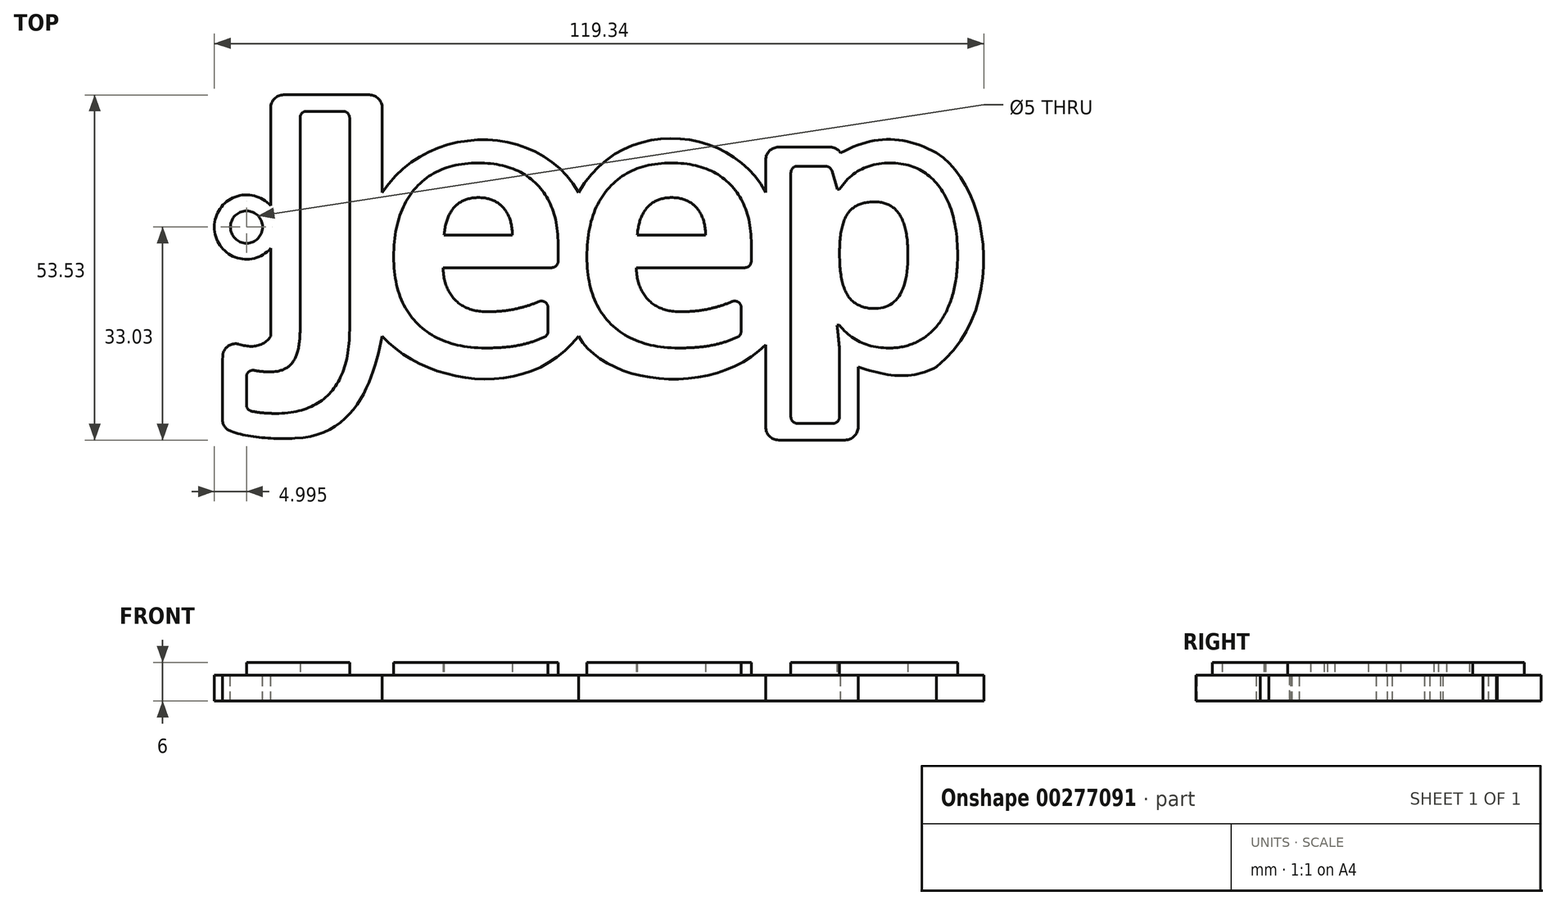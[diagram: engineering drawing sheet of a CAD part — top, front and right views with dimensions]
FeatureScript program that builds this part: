
annotation { "Feature Type Name" : "Feature", "Feature Type Description" : "" }
export const myFeature = defineFeature(function(context is Context, id is Id, definition is map)
    precondition{}
    {
        {
            var Q0;
            Q0=qCreatedBy(makeId("Top.planeOp"),FACE);
            var sketch = newSketch(context, id + "F0", { "sketchPlane" : qUnion([Q0])});
            skText(sketch, "E0", { "text": "Jeep", "fontName": "OpenSans-Bold.ttf"});
            skFitSpline(sketch, "E1", {"points": [v(-56.8, 0) * mm, v(-56.8, 20.5) * mm], "startDerivative": vector(0, 20.5) * mm, "endDerivative": vector(0, 20.5) * mm});
            skFitSpline(sketch, "E2", {"points": [v(-56.8, 20.5) * mm, v(-39.5, 20.5) * mm], "startDerivative": vector(15.4, 0) * mm, "endDerivative": vector(15.4, 0) * mm});
            skFitSpline(sketch, "E3", {"points": [v(-39.5, 5.36) * mm, v(-39.5, 20.5) * mm], "startDerivative": vector(0, 15.14) * mm, "endDerivative": vector(0, 15.14) * mm});
            skFitSpline(sketch, "E4", {"points": [v(-39.5, 5.36) * mm, v(-9.05, 5.36) * mm], "startDerivative": vector(21.09, 32.44) * mm, "endDerivative": vector(18.36, -32.95) * mm});
            skFitSpline(sketch, "E5", {"points": [v(-9.05, 5.36) * mm, v(19.99, 5.36) * mm], "startDerivative": vector(20.19, 35.94) * mm, "endDerivative": vector(16.2, -31.1) * mm});
            skFitSpline(sketch, "E6", {"points": [v(19.99, 5.36) * mm, v(19.99, 12.4) * mm], "startDerivative": vector(0, 7.03) * mm, "endDerivative": vector(0, 7.03) * mm});
            skFitSpline(sketch, "E7", {"points": [v(19.99, 12.4) * mm, v(31.61, 12.4) * mm], "startDerivative": vector(11.63, 0) * mm, "endDerivative": vector(11.63, 0) * mm});
            skFitSpline(sketch, "E8", {"points": [v(31.61, 12.4) * mm, v(31.61, 11.04) * mm], "startDerivative": vector(0, -1.35) * mm, "endDerivative": vector(0, -1.35) * mm});
            skFitSpline(sketch, "E9", {"points": [v(31.61, 11.5) * mm, v(46.48, 11.5) * mm], "startDerivative": vector(15.41, 8.38) * mm, "endDerivative": vector(15.41, -8.38) * mm});
            skFitSpline(sketch, "E10", {"points": [v(46.48, 11.5) * mm, v(46.48, -21.68) * mm], "startDerivative": vector(24.33, -15.14) * mm, "endDerivative": vector(-33.84, -27.42) * mm});
            skFitSpline(sketch, "E11", {"points": [v(46.48, -21.68) * mm, v(34.32, -21.68) * mm], "startDerivative": vector(-10.86, -6.04) * mm, "endDerivative": vector(-13.79, 4.87) * mm});
            skFitSpline(sketch, "E12", {"points": [v(34.32, -21.68) * mm, v(34.32, -33.03) * mm], "startDerivative": vector(0, -11.36) * mm, "endDerivative": vector(0, -11.36) * mm});
            skFitSpline(sketch, "E13", {"points": [v(34.32, -33.03) * mm, v(19.99, -33.03) * mm], "startDerivative": vector(-14.33, 0) * mm, "endDerivative": vector(-14.33, 0) * mm});
            skFitSpline(sketch, "E14", {"points": [v(19.99, -33.03) * mm, v(19.99, -18.26) * mm], "startDerivative": vector(0, 14.77) * mm, "endDerivative": vector(0, 14.77) * mm});
            skFitSpline(sketch, "E15", {"points": [v(19.99, -18.26) * mm, v(-9.05, -16.94) * mm], "startDerivative": vector(-23.52, -24.04) * mm, "endDerivative": vector(-13.5, 23.5) * mm});
            skFitSpline(sketch, "E16", {"points": [v(-9.05, -16.94) * mm, v(-39.5, -16.94) * mm], "startDerivative": vector(-22.79, -29.43) * mm, "endDerivative": vector(-21.9, 23.52) * mm});
            skFitSpline(sketch, "E17", {"points": [v(-39.5, -16.94) * mm, v(-53.01, -32.76) * mm], "startDerivative": vector(-4.06, -19.47) * mm, "endDerivative": vector(-29.09, -1.3) * mm});
            skFitSpline(sketch, "E18", {"points": [v(-53.01, -32.76) * mm, v(-64.27, -31.14) * mm], "startDerivative": vector(-13.04, -0.66) * mm, "endDerivative": vector(-8.11, 4.06) * mm});
            skFitSpline(sketch, "E19", {"points": [v(-64.27, -31.14) * mm, v(-64.27, -16.94) * mm], "startDerivative": vector(-0.27, 11.09) * mm, "endDerivative": vector(-0.27, 11.09) * mm});
            skFitSpline(sketch, "E20", {"points": [v(-64.27, -16.94) * mm, v(-56.8, -16.94) * mm], "startDerivative": vector(6.49, -4.06) * mm, "endDerivative": vector(5.7, 8.11) * mm});
            skFitSpline(sketch, "E21", {"points": [v(-56.8, -16.94) * mm, v(-56.8, 0) * mm], "startDerivative": vector(0, 19.51) * mm, "endDerivative": vector(0, 19.51) * mm});
            skCircle(sketch, "E22", {"center": v(-60.54, 0) * mm, "radius": 5 * mm});
            skCircle(sketch, "E23", {"center": v(-60.54, 0) * mm, "radius": 2.5 * mm});
            skLineSegment(sketch, "E24", {"start": v(-58.04, 0) * mm, "end": v(-55.54, 0) * mm});
            const initialGuessF0  = {"E0": [-0.0568, -0.01826, 1, 0, 0.03652]};
            skSetInitialGuess(sketch, initialGuessF0);
            skSolve(sketch);
        }
        {
            var Q0;
            Q0=makeQuery(id+"F0.imprint","IMPRINT",FACE,{"disambiguationData":[TD([[makeQuery(id+"F0.imprint","IMPRINT",EDGE,{"derivedFrom":sQuery(id+"F0.wireOp",EDGE,"E0.sketch_text.stroke-0")}),1.0]])]});
            var Q1;
            Q1=makeQuery(id+"F0.imprint","IMPRINT",FACE,{"disambiguationData":[TD([[makeQuery(id+"F0.imprint","IMPRINT",EDGE,{"derivedFrom":sQuery(id+"F0.wireOp",EDGE,"E0.sketch_text.stroke-0")}),-1.0]])]});
            var Q2;
            Q2=makeQuery(id+"F0.imprint","IMPRINT",FACE,{"disambiguationData":[TD([[makeQuery(id+"F0.imprint","IMPRINT",EDGE,{"derivedFrom":sQuery(id+"F0.wireOp",EDGE,"E0.sketch_text.stroke-10")}),-1.0]])]});
            var Q3;
            Q3=makeQuery(id+"F0.imprint","IMPRINT",FACE,{"disambiguationData":[TD([[makeQuery(id+"F0.imprint","IMPRINT",EDGE,{"derivedFrom":sQuery(id+"F0.wireOp",EDGE,"E0.sketch_text.stroke-10")}),1.0]])]});
            var Q4;
            Q4=makeQuery(id+"F0.imprint","IMPRINT",FACE,{"disambiguationData":[TD([[makeQuery(id+"F0.imprint","IMPRINT",EDGE,{"derivedFrom":sQuery(id+"F0.wireOp",EDGE,"E0.sketch_text.stroke-30")}),-1.0]])]});
            var Q5;
            Q5=makeQuery(id+"F0.imprint","IMPRINT",FACE,{"disambiguationData":[TD([[makeQuery(id+"F0.imprint","IMPRINT",EDGE,{"derivedFrom":sQuery(id+"F0.wireOp",EDGE,"E0.sketch_text.stroke-30")}),1.0]])]});
            var Q6;
            Q6=makeQuery(id+"F0.imprint","IMPRINT",FACE,{"disambiguationData":[TD([[makeQuery(id+"F0.imprint","IMPRINT",EDGE,{"derivedFrom":sQuery(id+"F0.wireOp",EDGE,"E0.sketch_text.stroke-50")}),-1.0]])]});
            var Q7;
            Q7=makeQuery(id+"F0.imprint","IMPRINT",FACE,{"disambiguationData":[TD([[makeQuery(id+"F0.imprint","IMPRINT",EDGE,{"derivedFrom":sQuery(id+"F0.wireOp",EDGE,"E0.sketch_text.stroke-65")}),1.0]])]});
            var Q8;
            Q8=makeQuery(id+"F0.imprint","IMPRINT",FACE,{"disambiguationData":[TD([[makeQuery(id+"F0.imprint","IMPRINT",EDGE,{"derivedFrom":sQuery(id+"F0.wireOp",EDGE,"E23")}),-1.0]])]});
            var Q9;
            {var subQ0=sQuery(id+"F0.wireOp",EDGE,"E21");var subQ1=sQuery(id+"F0.wireOp",EDGE,"E1");var subQ2=makeQuery(id+"F0.imprint","INTERSECT",VERTEX,{"derivedFrom":[subQ1,subQ0]});Q9=makeQuery(id+"F0.imprint","IMPRINT",FACE,{"disambiguationData":[TD([[makeQuery(id+"F0.imprint","IMPRINT",EDGE,{"disambiguationData":[TD([[subQ2,-1.0]])],"derivedFrom":subQ1}),-1.0]])]});}
            var Q10;
            {var subQ0=sQuery(id+"F0.wireOp",EDGE,"E24");var subQ3=sQuery(id+"F0.wireOp",EDGE,"E22");var subQ5=makeQuery(id+"F0.imprint","INTERSECT",VERTEX,{"derivedFrom":[subQ3,subQ0]});Q10=makeQuery(id+"F0.imprint","IMPRINT",FACE,{"disambiguationData":[TD([[makeQuery(id+"F0.imprint","IMPRINT",EDGE,{"disambiguationData":[TD([[subQ5,1.0]])],"derivedFrom":subQ3}),1.0]])]});}
            extrude(context, id + "F1", {"entities" : qUnion([Q0, Q1, Q2, Q3, Q4, Q5, Q6, Q7, Q8, Q9, Q10]), "oppositeDirection" : true, "depth" : 4 * mm});
        }
        {
            var Q0;
            Q0=makeQuery(id+"F0.imprint","IMPRINT",FACE,{"disambiguationData":[TD([[makeQuery(id+"F0.imprint","IMPRINT",EDGE,{"derivedFrom":sQuery(id+"F0.wireOp",EDGE,"E0.sketch_text.stroke-10")}),-1.0]])]});
            var Q1;
            Q1=makeQuery(id+"F0.imprint","IMPRINT",FACE,{"disambiguationData":[TD([[makeQuery(id+"F0.imprint","IMPRINT",EDGE,{"derivedFrom":sQuery(id+"F0.wireOp",EDGE,"E0.sketch_text.stroke-30")}),-1.0]])]});
            var Q2;
            Q2=makeQuery(id+"F0.imprint","IMPRINT",FACE,{"disambiguationData":[TD([[makeQuery(id+"F0.imprint","IMPRINT",EDGE,{"derivedFrom":sQuery(id+"F0.wireOp",EDGE,"E0.sketch_text.stroke-50")}),-1.0]])]});
            var Q3;
            Q3=makeQuery(id+"F0.imprint","IMPRINT",FACE,{"disambiguationData":[TD([[makeQuery(id+"F0.imprint","IMPRINT",EDGE,{"derivedFrom":sQuery(id+"F0.wireOp",EDGE,"E0.sketch_text.stroke-0")}),-1.0]])]});
            extrude(context, id + "F2", {"entities" : qUnion([Q0, Q1, Q2, Q3]), "operationType" : NewBodyOperationType.ADD, "depth" : 2 * mm});
        }
        {
            var Q0;
            Q0=makeQuery(id+"F1.opExtrude","SWEPT_EDGE",EDGE,{"disambiguationData":[OSD([sQuery(id+"F0.wireOp",EDGE,"E19"),sQuery(id+"F0.wireOp",EDGE,"E20")])]});
            var Q1;
            Q1=makeQuery(id+"F1.opExtrude","SWEPT_EDGE",EDGE,{"disambiguationData":[OSD([sQuery(id+"F0.wireOp",EDGE,"E18"),sQuery(id+"F0.wireOp",EDGE,"E19")])]});
            var Q2;
            Q2=makeQuery(id+"F1.opExtrude","SWEPT_EDGE",EDGE,{"disambiguationData":[OSD([sQuery(id+"F0.wireOp",EDGE,"E1"),sQuery(id+"F0.wireOp",EDGE,"E2")])]});
            var Q3;
            Q3=makeQuery(id+"F1.opExtrude","SWEPT_EDGE",EDGE,{"disambiguationData":[OSD([sQuery(id+"F0.wireOp",EDGE,"E2"),sQuery(id+"F0.wireOp",EDGE,"E3")])]});
            var Q4;
            Q4=makeQuery(id+"F1.opExtrude","SWEPT_EDGE",EDGE,{"disambiguationData":[OSD([sQuery(id+"F0.wireOp",EDGE,"E7"),sQuery(id+"F0.wireOp",EDGE,"E8")])]});
            var Q5;
            Q5=makeQuery(id+"F1.opExtrude","SWEPT_EDGE",EDGE,{"disambiguationData":[OSD([sQuery(id+"F0.wireOp",EDGE,"E6"),sQuery(id+"F0.wireOp",EDGE,"E7")])]});
            var Q6;
            Q6=makeQuery(id+"F1.opExtrude","SWEPT_EDGE",EDGE,{"disambiguationData":[OSD([sQuery(id+"F0.wireOp",EDGE,"E12"),sQuery(id+"F0.wireOp",EDGE,"E13")])]});
            var Q7;
            Q7=makeQuery(id+"F1.opExtrude","SWEPT_EDGE",EDGE,{"disambiguationData":[OSD([sQuery(id+"F0.wireOp",EDGE,"E13"),sQuery(id+"F0.wireOp",EDGE,"E14")])]});
            fillet(context, id + "F3", {"entities" : qUnion([Q0, Q1, Q2, Q3, Q4, Q5, Q6, Q7]), "radius" : 2 * mm, "tangentPropagation" : true, "allowEdgeOverflow" : false});
        }
        {
            var Q0;
            Q0=makeQuery(id+"F2.opExtrude","SWEPT_EDGE",EDGE,{"disambiguationData":[OSD([sQuery(id+"F0.wireOp",EDGE,"E0.sketch_text.stroke-54"),sQuery(id+"F0.wireOp",EDGE,"E0.sketch_text.stroke-55")])]});
            var Q1;
            Q1=makeQuery(id+"F2.opExtrude","SWEPT_EDGE",EDGE,{"disambiguationData":[OSD([sQuery(id+"F0.wireOp",EDGE,"E0.sketch_text.stroke-53"),sQuery(id+"F0.wireOp",EDGE,"E0.sketch_text.stroke-54")])]});
            var Q2;
            Q2=makeQuery(id+"F2.opExtrude","SWEPT_EDGE",EDGE,{"disambiguationData":[OSD([sQuery(id+"F0.wireOp",EDGE,"E0.sketch_text.stroke-56"),sQuery(id+"F0.wireOp",EDGE,"E0.sketch_text.stroke-57")])]});
            var Q3;
            Q3=makeQuery(id+"F2.opExtrude","SWEPT_EDGE",EDGE,{"disambiguationData":[OSD([sQuery(id+"F0.wireOp",EDGE,"E0.sketch_text.stroke-55"),sQuery(id+"F0.wireOp",EDGE,"E0.sketch_text.stroke-56")])]});
            var Q4;
            Q4=makeQuery(id+"F2.opExtrude","SWEPT_EDGE",EDGE,{"disambiguationData":[OSD([sQuery(id+"F0.wireOp",EDGE,"E0.sketch_text.stroke-41"),sQuery(id+"F0.wireOp",EDGE,"E0.sketch_text.stroke-42")])]});
            var Q5;
            Q5=makeQuery(id+"F2.opExtrude","SWEPT_EDGE",EDGE,{"disambiguationData":[OSD([sQuery(id+"F0.wireOp",EDGE,"E0.sketch_text.stroke-46"),sQuery(id+"F0.wireOp",EDGE,"E0.sketch_text.stroke-47")])]});
            var Q6;
            Q6=makeQuery(id+"F2.opExtrude","SWEPT_EDGE",EDGE,{"disambiguationData":[OSD([sQuery(id+"F0.wireOp",EDGE,"E0.sketch_text.stroke-47"),sQuery(id+"F0.wireOp",EDGE,"E0.sketch_text.stroke-48")])]});
            var Q7;
            Q7=makeQuery(id+"F2.opExtrude","SWEPT_EDGE",EDGE,{"disambiguationData":[OSD([sQuery(id+"F0.wireOp",EDGE,"E0.sketch_text.stroke-27"),sQuery(id+"F0.wireOp",EDGE,"E0.sketch_text.stroke-28")])]});
            var Q8;
            Q8=makeQuery(id+"F2.opExtrude","SWEPT_EDGE",EDGE,{"disambiguationData":[OSD([sQuery(id+"F0.wireOp",EDGE,"E0.sketch_text.stroke-21"),sQuery(id+"F0.wireOp",EDGE,"E0.sketch_text.stroke-22")])]});
            var Q9;
            Q9=makeQuery(id+"F2.opExtrude","SWEPT_EDGE",EDGE,{"disambiguationData":[OSD([sQuery(id+"F0.wireOp",EDGE,"E0.sketch_text.stroke-26"),sQuery(id+"F0.wireOp",EDGE,"E0.sketch_text.stroke-27")])]});
            var Q10;
            Q10=makeQuery(id+"F2.opExtrude","SWEPT_EDGE",EDGE,{"disambiguationData":[OSD([sQuery(id+"F0.wireOp",EDGE,"E0.sketch_text.stroke-5"),sQuery(id+"F0.wireOp",EDGE,"E0.sketch_text.stroke-6")])]});
            var Q11;
            Q11=makeQuery(id+"F2.opExtrude","SWEPT_EDGE",EDGE,{"disambiguationData":[OSD([sQuery(id+"F0.wireOp",EDGE,"E0.sketch_text.stroke-6"),sQuery(id+"F0.wireOp",EDGE,"E0.sketch_text.stroke-7")])]});
            var Q12;
            Q12=makeQuery(id+"F2.opExtrude","SWEPT_EDGE",EDGE,{"disambiguationData":[OSD([sQuery(id+"F0.wireOp",EDGE,"E0.sketch_text.stroke-1"),sQuery(id+"F0.wireOp",EDGE,"E0.sketch_text.stroke-2")])]});
            var Q13;
            Q13=makeQuery(id+"F2.opExtrude","SWEPT_EDGE",EDGE,{"disambiguationData":[OSD([sQuery(id+"F0.wireOp",EDGE,"E0.sketch_text.stroke-0"),sQuery(id+"F0.wireOp",EDGE,"E0.sketch_text.stroke-1")])]});
            fillet(context, id + "F4", {"entities" : qUnion([Q0, Q1, Q2, Q3, Q4, Q5, Q6, Q7, Q8, Q9, Q10, Q11, Q12, Q13]), "radius" : 1 * mm, "tangentPropagation" : true, "allowEdgeOverflow" : false});
        }
    });
